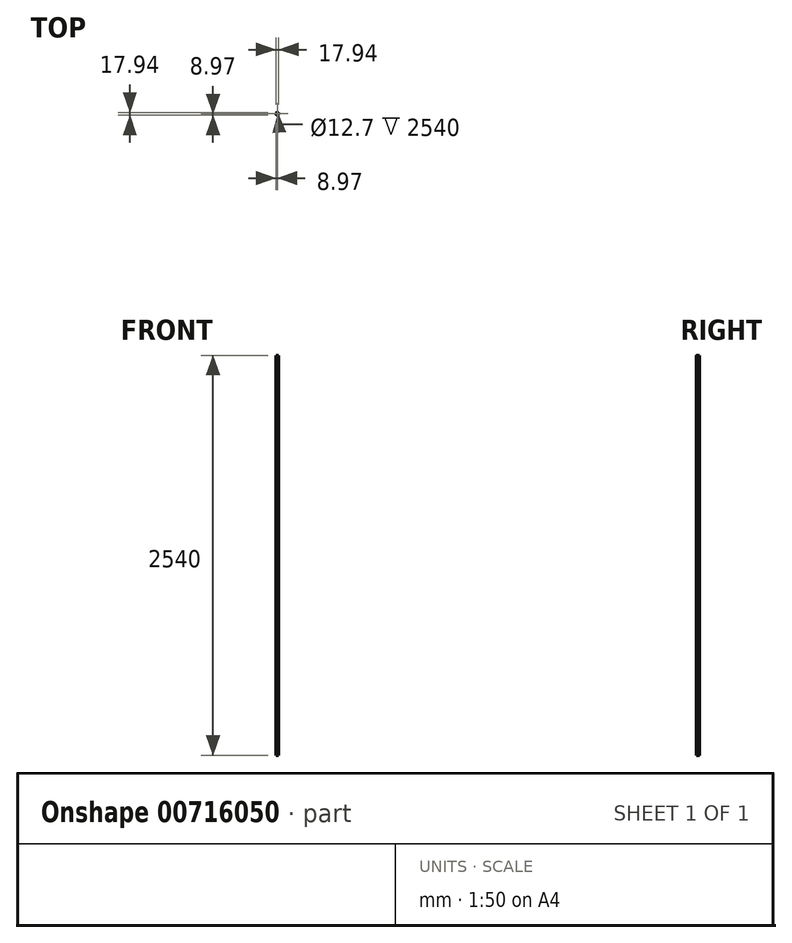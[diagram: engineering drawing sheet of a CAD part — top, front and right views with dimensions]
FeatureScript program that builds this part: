
annotation { "Feature Type Name" : "Feature", "Feature Type Description" : "" }
export const myFeature = defineFeature(function(context is Context, id is Id, definition is map)
    precondition{}
    {
        {
            var Q0;
            Q0=qCreatedBy(makeId("Top.planeOp"),FACE);
            var sketch = newSketch(context, id + "F0", { "sketchPlane" : qUnion([Q0])});
            skCircle(sketch, "E0", {"center": v(0, 0) * mm, "radius": 8.97 * mm});
            skCircle(sketch, "E1", {"center": v(0, 0) * mm, "radius": 6.35 * mm});
            skSolve(sketch);
        }
        {
            var Q0;
            Q0 = qSketchRegion(id + "F0", true);
            extrude(context, id + "F1", {"entities" : qUnion([Q0]), "depth" : 2540 * mm, "offsetDistance" : 25.4 * mm});
        }
    });
